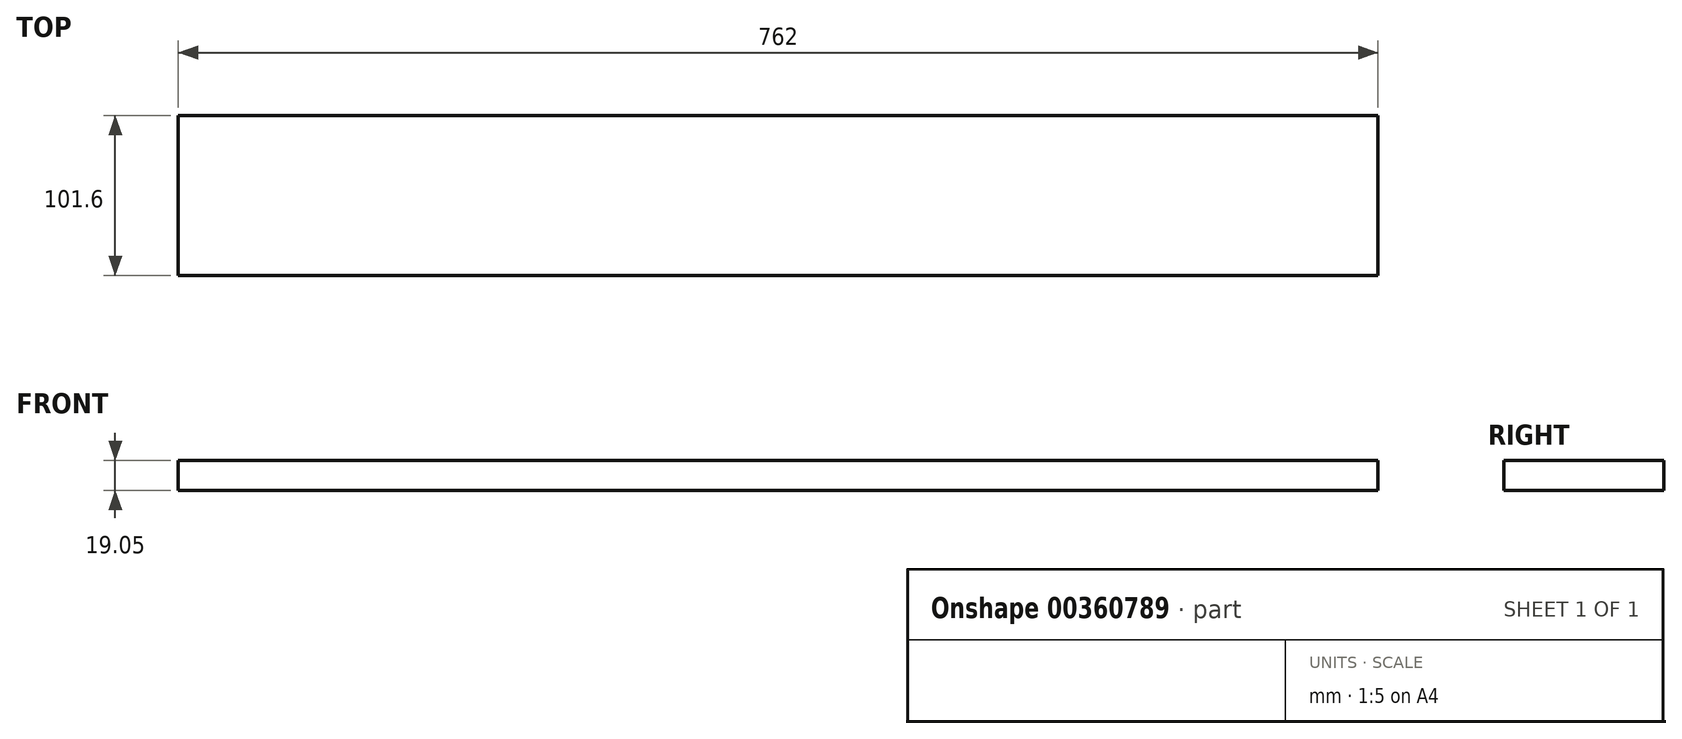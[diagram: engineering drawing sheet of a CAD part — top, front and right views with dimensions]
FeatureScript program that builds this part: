
annotation { "Feature Type Name" : "Feature", "Feature Type Description" : "" }
export const myFeature = defineFeature(function(context is Context, id is Id, definition is map)
    precondition{}
    {
        {
            var Q0;
            Q0=qCreatedBy(makeId("Top.planeOp"),FACE);
            var sketch = newSketch(context, id + "F0", { "sketchPlane" : qUnion([Q0])});
            skLineSegment(sketch, "E0.bottom", {"start": v(0, 0) * mm, "end": v(762, 0) * mm});
            skLineSegment(sketch, "E0.top", {"start": v(0, 101.6) * mm, "end": v(762, 101.6) * mm});
            skLineSegment(sketch, "E0.left", {"start": v(0, 0) * mm, "end": v(0, 101.6) * mm});
            skLineSegment(sketch, "E0.right", {"start": v(762, 0) * mm, "end": v(762, 101.6) * mm});
            skSolve(sketch);
        }
        {
            var Q0;
            Q0=makeQuery(id+"F0.imprint","IMPRINT",FACE,{"disambiguationData":[TD([[makeQuery(id+"F0.imprint","IMPRINT",EDGE,{"derivedFrom":sQuery(id+"F0.wireOp",EDGE,"E0.bottom")}),1.0]])]});
            extrude(context, id + "F1", {"entities" : qUnion([Q0]), "depth" : 19.05 * mm});
        }
    });
